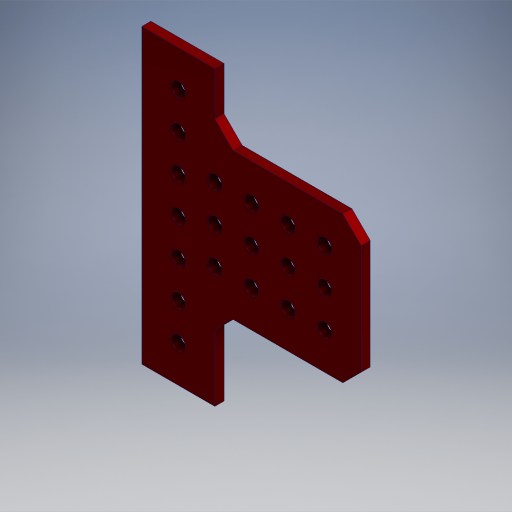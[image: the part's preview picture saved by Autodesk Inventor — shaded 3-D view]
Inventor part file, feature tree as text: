
AUTODESK INVENTOR PART (.ipt)
format: ipt  version: 2024.2 (Build 282272000, 272)  size: 350,720 bytes
history: native  units: in
note: dims shown in document units (in); Inventor stores cm internally (conversion verified against a paired STEP export)
features: extrude x1, sketch x1
ambient origin geometry x8: Origin, YZ Plane, XZ Plane, XY Plane, X Axis, Y Axis, Z Axis, Center Point
bodies: Body1 (feature_tree)
feature tree (2):
  extrude  "Extrusion2"  Depth=0.5in
  sketch  "Sketch1"  dims[d0=0.196in d1=0.196in d2=0.346in d3=0.5in d4=1.5748in d6=0.5in d7=0.3937in d9=1.0in d11=1.5748in d13=0.5in d14=0.3937in d16=1.0in d26=1.1811in d28=0.5in d29=0.3937in d31=1.0in d33=1.1811in d35=0.5in d36=0.3937in d38=1.0in d42=0.5in d43=0.5in d44=2.0in d45=0.654in d46=1.0in d47=3.5in d48=0.25in d49=0.25in d50=0.25in d51=0.25in d52=0.25in d53=0.25in d54=0.25in d55=0.25in d56=0.125in d57=0.0in d58=0.7874in d60=0.5in d61=0.3937in d63=1.0in d66=0.5in]
